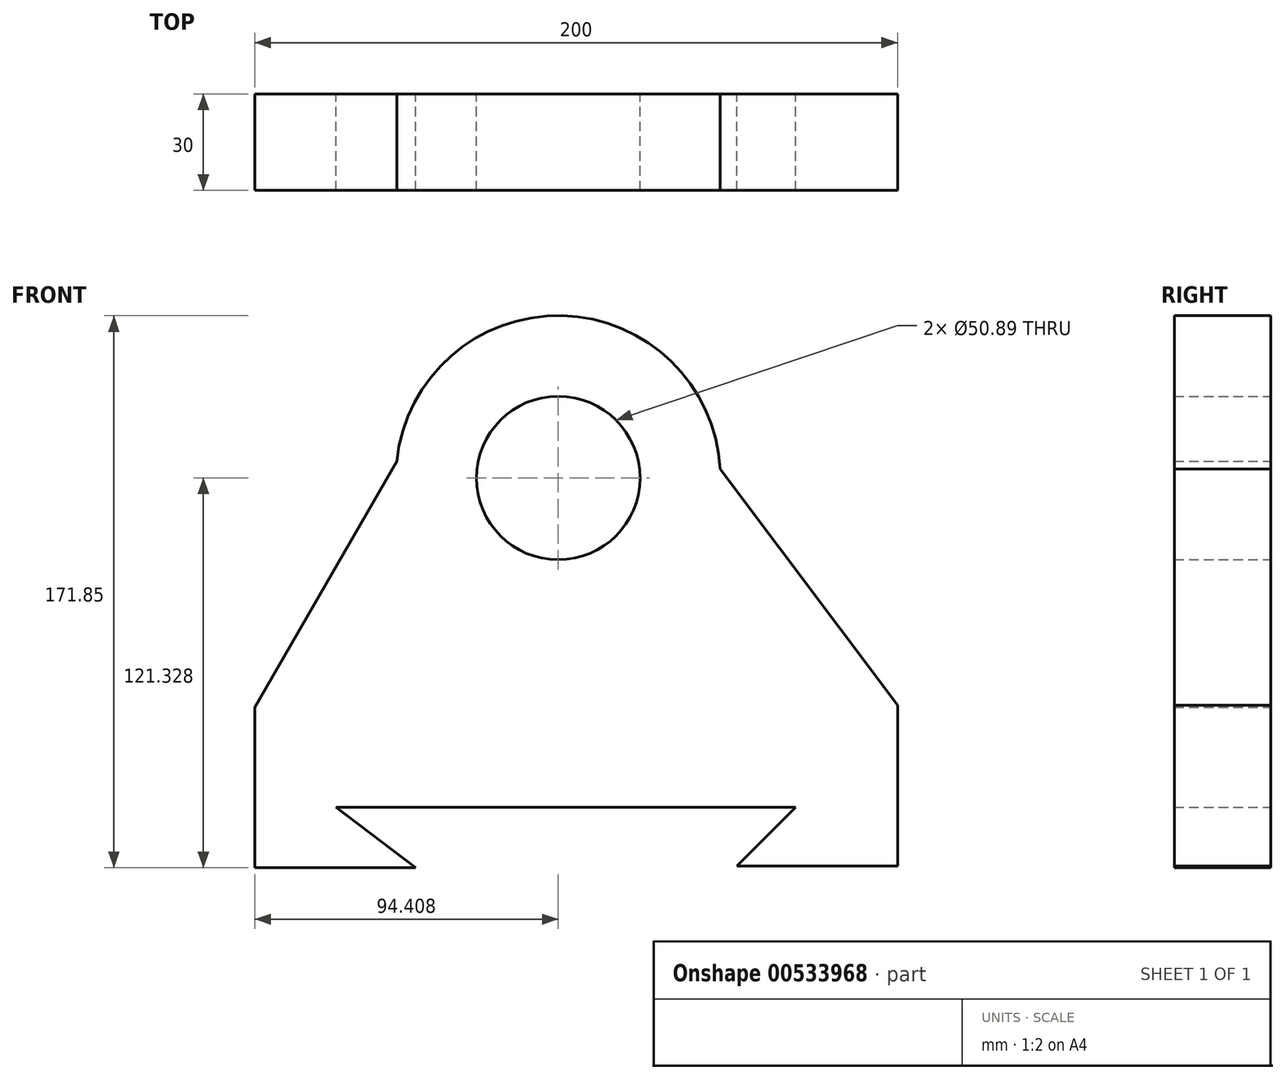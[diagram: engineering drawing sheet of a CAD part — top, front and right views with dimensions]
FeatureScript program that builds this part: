
annotation { "Feature Type Name" : "Feature", "Feature Type Description" : "" }
export const myFeature = defineFeature(function(context is Context, id is Id, definition is map)
    precondition{}
    {
        {
            var Q0;
            Q0=qCreatedBy(makeId("Front.planeOp"),FACE);
            var sketch = newSketch(context, id + "F0", { "sketchPlane" : qUnion([Q0])});
            skLineSegment(sketch, "E0", {"start": v(-139.25, 31.18) * mm, "end": v(-139.25, -18.82) * mm});
            skLineSegment(sketch, "E1", {"start": v(-139.25, -18.82) * mm, "end": v(-89.25, -18.82) * mm});
            skLineSegment(sketch, "E2", {"start": v(-89.25, -18.82) * mm, "end": v(-113.98, 0) * mm});
            skLineSegment(sketch, "E3", {"start": v(-113.98, 0) * mm, "end": v(29.02, 0) * mm});
            skLineSegment(sketch, "E4", {"start": v(29.02, 0) * mm, "end": v(10.75, -18.25) * mm});
            skLineSegment(sketch, "E5", {"start": v(10.75, -18.25) * mm, "end": v(60.75, -18.25) * mm});
            skLineSegment(sketch, "E6", {"start": v(60.75, -18.25) * mm, "end": v(60.75, 31.75) * mm});
            skLineSegment(sketch, "E7", {"start": v(60.75, 31.75) * mm, "end": v(-139.25, 31.18) * mm});
            skCircle(sketch, "E8", {"center": v(-44.84, 102.5) * mm, "radius": 25.45 * mm});
            skCircle(sketch, "E9", {"center": v(-44.84, 102.5) * mm, "radius": 50.52 * mm});
            skLineSegment(sketch, "E10", {"start": v(-139.25, 31.18) * mm, "end": v(-95.09, 107.78) * mm});
            skLineSegment(sketch, "E11", {"start": v(60.75, 31.75) * mm, "end": v(5.6, 105.3) * mm});
            skSolve(sketch);
        }
        {
            var Q0;
            Q0 = qSketchRegion(id + "F0", true);
            extrude(context, id + "F1", {"entities" : qUnion([Q0]), "depth" : 30 * mm, "offsetDistance" : 25 * mm});
        }
    });
